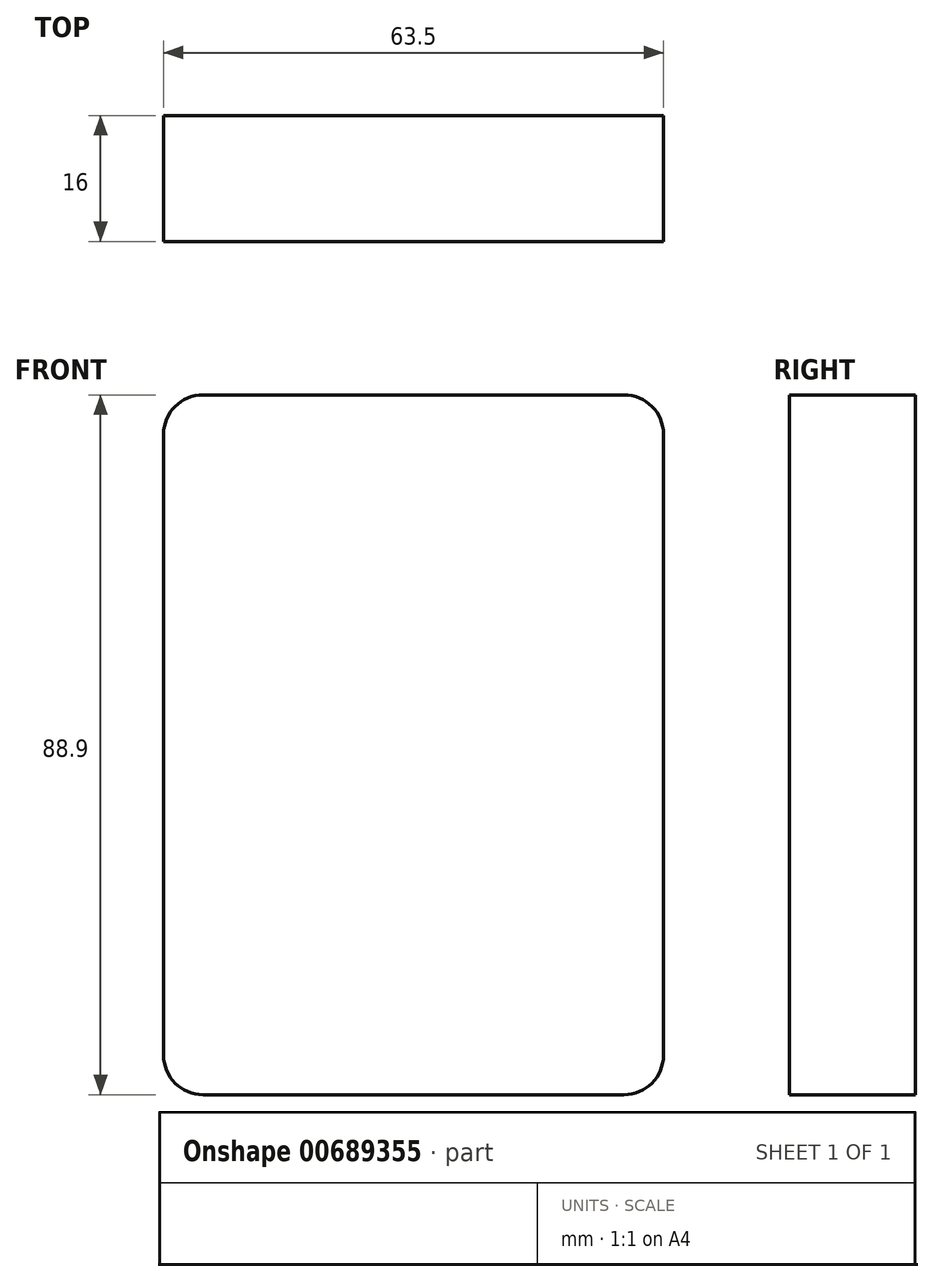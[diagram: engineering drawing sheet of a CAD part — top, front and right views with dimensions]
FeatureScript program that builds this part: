
annotation { "Feature Type Name" : "Feature", "Feature Type Description" : "" }
export const myFeature = defineFeature(function(context is Context, id is Id, definition is map)
    precondition{}
    {
        {
            var Q0;
            Q0=qCreatedBy(makeId("Front.planeOp"),FACE);
            var sketch = newSketch(context, id + "F0", { "sketchPlane" : qUnion([Q0])});
            skLineSegment(sketch, "E0.bottom", {"start": v(0, 0) * mm, "end": v(-63.5, 0) * mm});
            skLineSegment(sketch, "E0.top", {"start": v(0, 88.9) * mm, "end": v(-63.5, 88.9) * mm});
            skLineSegment(sketch, "E0.left", {"start": v(0, 0) * mm, "end": v(0, 88.9) * mm});
            skLineSegment(sketch, "E0.right", {"start": v(-63.5, 0) * mm, "end": v(-63.5, 88.9) * mm});
            skSolve(sketch);
        }
        {
            var Q0;
            Q0=qSketchRegion(id+"F0",true);
            extrude(context, id + "F1", {"entities" : qUnion([Q0]), "depth" : 16 * mm, "offsetDistance" : 25 * mm});
        }
        {
            var Q0;
            Q0=makeQuery(id+"F1.opExtrude","SWEPT_EDGE",EDGE,{"disambiguationData":[OSD([sQuery(id+"F0.wireOp",EDGE,"E0.top"),sQuery(id+"F0.wireOp",EDGE,"E0.right")])]});
            var Q1;
            Q1=makeQuery(id+"F1.opExtrude","SWEPT_EDGE",EDGE,{"disambiguationData":[OSD([sQuery(id+"F0.wireOp",EDGE,"E0.top"),sQuery(id+"F0.wireOp",EDGE,"E0.left")])]});
            var Q2;
            Q2=makeQuery(id+"F1.opExtrude","SWEPT_EDGE",EDGE,{"disambiguationData":[OSD([sQuery(id+"F0.wireOp",EDGE,"E0.bottom"),sQuery(id+"F0.wireOp",EDGE,"E0.left")])]});
            var Q3;
            Q3=makeQuery(id+"F1.opExtrude","SWEPT_EDGE",EDGE,{"disambiguationData":[OSD([sQuery(id+"F0.wireOp",EDGE,"E0.bottom"),sQuery(id+"F0.wireOp",EDGE,"E0.right")])]});
            fillet(context, id + "F2", {"entities" : qUnion([Q0, Q1, Q2, Q3]), "radius" : 5 * mm, "tangentPropagation" : true, "allowEdgeOverflow" : false});
        }
    });
